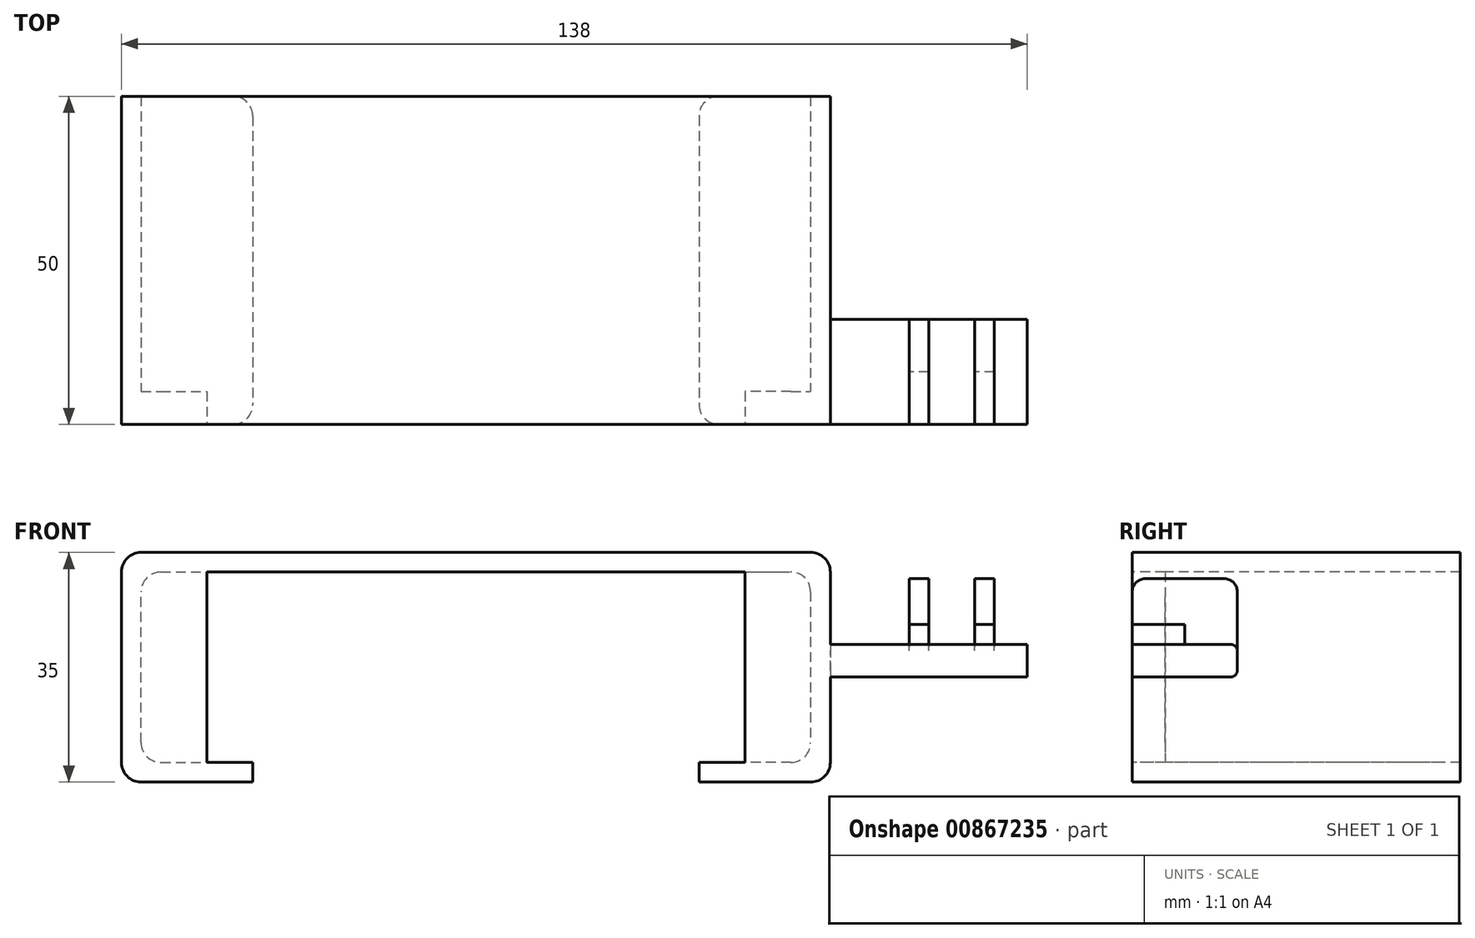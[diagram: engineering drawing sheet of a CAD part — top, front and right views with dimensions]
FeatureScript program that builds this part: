
annotation { "Feature Type Name" : "Feature", "Feature Type Description" : "" }
export const myFeature = defineFeature(function(context is Context, id is Id, definition is map)
    precondition{}
    {
        {
            var Q0;
            Q0=qCreatedBy(makeId("Top.planeOp"),FACE);
            var sketch = newSketch(context, id + "F0", { "sketchPlane" : qUnion([Q0])});
            skLineSegment(sketch, "E0.bottom", {"start": v(-6.5, 16) * mm, "end": v(-3.5, 16) * mm});
            skLineSegment(sketch, "E0.top", {"start": v(-6.5, 0) * mm, "end": v(-3.5, 0) * mm});
            skLineSegment(sketch, "E0.left", {"start": v(-6.5, 16) * mm, "end": v(-6.5, 0) * mm});
            skLineSegment(sketch, "E0.right", {"start": v(-3.5, 16) * mm, "end": v(-3.5, 0) * mm});
            skLineSegment(sketch, "E1.bottom", {"start": v(3.5, 16) * mm, "end": v(6.5, 16) * mm});
            skLineSegment(sketch, "E1.top", {"start": v(3.5, 0) * mm, "end": v(6.5, 0) * mm});
            skLineSegment(sketch, "E1.left", {"start": v(3.5, 16) * mm, "end": v(3.5, 0) * mm});
            skLineSegment(sketch, "E1.right", {"start": v(6.5, 16) * mm, "end": v(6.5, 0) * mm});
            skSolve(sketch);
        }
        {
            var Q0;
            Q0=makeQuery(id+"F0.imprint","IMPRINT",FACE,{"disambiguationData":[TD([[makeQuery(id+"F0.imprint","IMPRINT",EDGE,{"derivedFrom":sQuery(id+"F0.wireOp",EDGE,"E0.bottom")}),-1.0]])]});
            var Q1;
            Q1=makeQuery(id+"F0.imprint","IMPRINT",FACE,{"disambiguationData":[TD([[makeQuery(id+"F0.imprint","IMPRINT",EDGE,{"derivedFrom":sQuery(id+"F0.wireOp",EDGE,"E1.bottom")}),-1.0]])]});
            extrude(context, id + "F1", {"entities" : qUnion([Q0, Q1]), "depth" : 10 * mm, "offsetDistance" : 25 * mm});
        }
        {
            var Q0;
            Q0=makeQuery(id+"F1.opExtrude","SWEPT_FACE",FACE,{"disambiguationData":[OSD([sQuery(id+"F0.wireOp",EDGE,"E0.left")])]});
            var sketch = newSketch(context, id + "F2", { "sketchPlane" : qUnion([Q0])});
            skLineSegment(sketch, "E2.bottom", {"start": v(0, 0) * mm, "end": v(-8, 0) * mm});
            skLineSegment(sketch, "E2.top", {"start": v(0, 3) * mm, "end": v(-8, 3) * mm});
            skLineSegment(sketch, "E2.left", {"start": v(0, 0) * mm, "end": v(0, 3) * mm});
            skLineSegment(sketch, "E2.right", {"start": v(-8, 0) * mm, "end": v(-8, 3) * mm});
            skSolve(sketch);
        }
        {
            var Q0;
            Q0=makeQuery(id+"F2.imprint","IMPRINT",FACE,{"disambiguationData":[TD([[makeQuery(id+"F2.imprint","IMPRINT",EDGE,{"derivedFrom":sQuery(id+"F2.wireOp",EDGE,"E2.bottom")}),1.0]])]});
            extrude(context, id + "F3", {"entities" : qUnion([Q0]), "operationType" : NewBodyOperationType.REMOVE, "oppositeDirection" : true, "depth" : 25 * mm, "offsetDistance" : 25 * mm});
        }
        {
            var Q0;
            Q0=qCreatedBy(makeId("Top.planeOp"),FACE);
            var sketch = newSketch(context, id + "F4", { "sketchPlane" : qUnion([Q0])});
            skPoint(sketch, "E3.0", {"position": v(-6.5, 16) * mm});
            skPoint(sketch, "E4.0", {"position": v(-6.5, 0) * mm});
            skLineSegment(sketch, "E5.bottom", {"start": v(-18.5, 16) * mm, "end": v(11.5, 16) * mm});
            skLineSegment(sketch, "E5.top", {"start": v(-18.5, 0) * mm, "end": v(11.5, 0) * mm});
            skLineSegment(sketch, "E5.left", {"start": v(-18.5, 16) * mm, "end": v(-18.5, 0) * mm});
            skLineSegment(sketch, "E5.right", {"start": v(11.5, 16) * mm, "end": v(11.5, 0) * mm});
            skSolve(sketch);
        }
        {
            var Q0;
            Q0=makeQuery(id+"F4.imprint","IMPRINT",FACE,{"disambiguationData":[TD([[makeQuery(id+"F4.imprint","IMPRINT",EDGE,{"derivedFrom":sQuery(id+"F4.wireOp",EDGE,"E5.bottom")}),-1.0]])]});
            extrude(context, id + "F5", {"entities" : qUnion([Q0]), "operationType" : NewBodyOperationType.ADD, "oppositeDirection" : true, "depth" : 5 * mm, "offsetDistance" : 25 * mm});
        }
        {
            var Q0;
            Q0=qCreatedBy(makeId("Front.planeOp"),FACE);
            var sketch = newSketch(context, id + "F6", { "sketchPlane" : qUnion([Q0])});
            skPoint(sketch, "E6.0", {"position": v(11.5, -5) * mm});
            skPoint(sketch, "E7.0", {"position": v(11.5, 0) * mm});
            skLineSegment(sketch, "E8.right", {"start": v(-123.5, -18) * mm, "end": v(-123.5, 11) * mm});
            skLineSegment(sketch, "E9.bottom", {"start": v(-126.5, 14) * mm, "end": v(-18.5, 14) * mm});
            skLineSegment(sketch, "E9.top", {"start": v(-123.5, 11) * mm, "end": v(-21.5, 11) * mm});
            skLineSegment(sketch, "E10.left", {"start": v(-18.5, 14) * mm, "end": v(-18.5, -21) * mm});
            skLineSegment(sketch, "E10.right", {"start": v(-21.5, 11) * mm, "end": v(-21.5, -18) * mm});
            skLineSegment(sketch, "E11.bottom", {"start": v(-18.5, -21) * mm, "end": v(-38.5, -21) * mm});
            skLineSegment(sketch, "E11.top", {"start": v(-21.5, -18) * mm, "end": v(-38.5, -18) * mm});
            skLineSegment(sketch, "E11.right", {"start": v(-38.5, -21) * mm, "end": v(-38.5, -18) * mm});
            skLineSegment(sketch, "E12.bottom", {"start": v(-126.5, -21) * mm, "end": v(-106.5, -21) * mm});
            skLineSegment(sketch, "E12.top", {"start": v(-123.5, -18) * mm, "end": v(-106.5, -18) * mm});
            skLineSegment(sketch, "E12.right", {"start": v(-106.5, -21) * mm, "end": v(-106.5, -18) * mm});
            skLineSegment(sketch, "E13", {"start": v(-113.5, 11) * mm, "end": v(-113.5, -18) * mm});
            skLineSegment(sketch, "E14", {"start": v(-126.5, -21) * mm, "end": v(-126.5, 14) * mm});
            skLineSegment(sketch, "E15", {"start": v(-31.5, -18) * mm, "end": v(-31.5, 11) * mm});
            skSolve(sketch);
        }
        {
            var Q0;
            {var subQ7=sQuery(id+"F6.wireOp",EDGE,"E8.right");Q0=makeQuery(id+"F6.imprint","IMPRINT",FACE,{"disambiguationData":[TD([[makeQuery(id+"F6.imprint","IMPRINT",EDGE,{"derivedFrom":subQ7}),1.0]])]});}
            extrude(context, id + "F7", {"entities" : qUnion([Q0]), "operationType" : NewBodyOperationType.ADD, "oppositeDirection" : true, "depth" : 50 * mm, "offsetDistance" : 25 * mm});
        }
        {
            var Q0;
            {var subQ0=sQuery(id+"F6.wireOp",EDGE,"E10.right");Q0=makeQuery(id+"F6.imprint","IMPRINT",FACE,{"disambiguationData":[TD([[makeQuery(id+"F6.imprint","IMPRINT",EDGE,{"derivedFrom":subQ0}),-1.0]])]});}
            var Q1;
            {var subQ0=sQuery(id+"F6.wireOp",EDGE,"E8.right");Q1=makeQuery(id+"F6.imprint","IMPRINT",FACE,{"disambiguationData":[TD([[makeQuery(id+"F6.imprint","IMPRINT",EDGE,{"derivedFrom":subQ0}),-1.0]])]});}
            extrude(context, id + "F8", {"entities" : qUnion([Q0, Q1]), "operationType" : NewBodyOperationType.ADD, "oppositeDirection" : true, "depth" : 5 * mm, "offsetDistance" : 25 * mm});
        }
        {
            var Q0;
            Q0=makeQuery(id+"F1.opExtrude","CAP_EDGE",EDGE,{"disambiguationData":[OSD([sQuery(id+"F0.wireOp",EDGE,"E0.bottom")])],"isStart":false});
            var Q1;
            Q1=makeQuery(id+"F1.opExtrude","CAP_EDGE",EDGE,{"disambiguationData":[OSD([sQuery(id+"F0.wireOp",EDGE,"E1.bottom")])],"isStart":false});
            var Q2;
            Q2=makeQuery(id+"F1.opExtrude","CAP_EDGE",EDGE,{"disambiguationData":[OSD([sQuery(id+"F0.wireOp",EDGE,"E0.top")])],"isStart":false});
            var Q3;
            Q3=makeQuery(id+"F1.opExtrude","CAP_EDGE",EDGE,{"disambiguationData":[OSD([sQuery(id+"F0.wireOp",EDGE,"E1.top")])],"isStart":false});
            var Q4;
            {var subQ0=sQuery(id+"F0.wireOp",EDGE,"E0.top");var subQ1=sQuery(id+"F2.wireOp",EDGE,"E2.top");Q4=makeQuery(id+"F3.boolean.opBoolean","COPY",EDGE,{"disambiguationData":[topologyDisambiguationEdgeConnected([makeQuery(id+"F1.opExtrude","SWEPT_FACE",FACE,{"disambiguationData":[OSD([subQ0])]})])],"derivedFrom":makeQuery(id+"F3.opExtrude","SWEPT_EDGE",EDGE,{"disambiguationData":[OSD([subQ0,sQuery(id+"F0.wireOp",EDGE,"E0.left"),subQ1,sQuery(id+"F2.wireOp",EDGE,"E2.left")])]})});}
            var Q5;
            {var subQ0=sQuery(id+"F2.wireOp",EDGE,"E2.top");Q5=makeQuery(id+"F3.boolean.opBoolean","COPY",EDGE,{"disambiguationData":[topologyDisambiguationEdgeConnected([makeQuery(id+"F1.opExtrude","SWEPT_FACE",FACE,{"disambiguationData":[OSD([sQuery(id+"F0.wireOp",EDGE,"E1.top")])]})])],"derivedFrom":makeQuery(id+"F3.opExtrude","SWEPT_EDGE",EDGE,{"disambiguationData":[OSD([sQuery(id+"F0.wireOp",EDGE,"E0.top"),sQuery(id+"F0.wireOp",EDGE,"E0.left"),subQ0,sQuery(id+"F2.wireOp",EDGE,"E2.left")])]})});}
            fillet(context, id + "F9", {"entities" : qUnion([Q0, Q1, Q2, Q3, Q4, Q5]), "radius" : 2 * mm, "tangentPropagation" : true, "allowEdgeOverflow" : false});
        }
        {
            var Q0;
            Q0=makeQuery(id+"F7.opExtrude","SWEPT_EDGE",EDGE,{"disambiguationData":[OSD([sQuery(id+"F6.wireOp",EDGE,"E9.top"),sQuery(id+"F6.wireOp",EDGE,"E10.right")])]});
            var Q1;
            Q1=makeQuery(id+"F7.opExtrude","SWEPT_EDGE",EDGE,{"disambiguationData":[OSD([sQuery(id+"F6.wireOp",EDGE,"E8.right"),sQuery(id+"F6.wireOp",EDGE,"E9.top")])]});
            var Q2;
            Q2=makeQuery(id+"F7.opExtrude","SWEPT_EDGE",EDGE,{"disambiguationData":[OSD([sQuery(id+"F6.wireOp",EDGE,"E9.bottom"),sQuery(id+"F6.wireOp",EDGE,"E14")])]});
            var Q3;
            Q3=makeQuery(id+"F7.opExtrude","SWEPT_EDGE",EDGE,{"disambiguationData":[OSD([sQuery(id+"F6.wireOp",EDGE,"E9.bottom"),sQuery(id+"F6.wireOp",EDGE,"E10.left")])]});
            var Q4;
            Q4=makeQuery(id+"F7.opExtrude","SWEPT_EDGE",EDGE,{"disambiguationData":[OSD([sQuery(id+"F6.wireOp",EDGE,"E10.left"),sQuery(id+"F6.wireOp",EDGE,"E11.bottom")])]});
            var Q5;
            Q5=makeQuery(id+"F7.opExtrude","SWEPT_EDGE",EDGE,{"disambiguationData":[OSD([sQuery(id+"F6.wireOp",EDGE,"E10.right"),sQuery(id+"F6.wireOp",EDGE,"E11.top")])]});
            var Q6;
            Q6=makeQuery(id+"F7.opExtrude","SWEPT_EDGE",EDGE,{"disambiguationData":[OSD([sQuery(id+"F6.wireOp",EDGE,"E8.right"),sQuery(id+"F6.wireOp",EDGE,"E12.top")])]});
            var Q7;
            Q7=makeQuery(id+"F7.opExtrude","SWEPT_EDGE",EDGE,{"disambiguationData":[OSD([sQuery(id+"F6.wireOp",EDGE,"E12.bottom"),sQuery(id+"F6.wireOp",EDGE,"E14")])]});
            var Q8;
            Q8=makeQuery(id+"F8.opExtrude","CAP_EDGE",EDGE,{"disambiguationData":[OSD([sQuery(id+"F6.wireOp",EDGE,"E8.right")])],"isStart":false});
            var Q9;
            Q9=makeQuery(id+"F8.opExtrude","CAP_EDGE",EDGE,{"disambiguationData":[OSD([sQuery(id+"F6.wireOp",EDGE,"E12.top")])],"isStart":false});
            var Q10;
            Q10=makeQuery(id+"F8.opExtrude","CAP_EDGE",EDGE,{"disambiguationData":[OSD([sQuery(id+"F6.wireOp",EDGE,"E11.top")])],"isStart":false});
            var Q11;
            Q11=makeQuery(id+"F8.opExtrude","CAP_EDGE",EDGE,{"disambiguationData":[OSD([sQuery(id+"F6.wireOp",EDGE,"E10.right")])],"isStart":false});
            var Q12;
            {var subQ0=sQuery(id+"F6.wireOp",EDGE,"E9.top");Q12=makeQuery(id+"F8.opExtrude","CAP_EDGE",EDGE,{"disambiguationData":[OSD([subQ0]),TDD([makeQuery(id+"F6.imprint","IMPRINT",EDGE,{"disambiguationData":[TD([[makeQuery(id+"F6.imprint","INTERSECT",VERTEX,{"derivedFrom":[subQ0,sQuery(id+"F6.wireOp",EDGE,"E10.right")]}),1.0]])],"derivedFrom":subQ0})])],"isStart":false});}
            var Q13;
            {var subQ0=sQuery(id+"F6.wireOp",EDGE,"E9.top");Q13=makeQuery(id+"F8.opExtrude","CAP_EDGE",EDGE,{"disambiguationData":[OSD([subQ0]),TDD([makeQuery(id+"F6.imprint","IMPRINT",EDGE,{"disambiguationData":[TD([[makeQuery(id+"F6.imprint","INTERSECT",VERTEX,{"derivedFrom":[sQuery(id+"F6.wireOp",EDGE,"E8.right"),subQ0]}),-1.0]])],"derivedFrom":subQ0})])],"isStart":false});}
            var Q14;
            Q14=makeQuery(id+"F7.opExtrude","CAP_EDGE",EDGE,{"disambiguationData":[OSD([sQuery(id+"F6.wireOp",EDGE,"E11.right")])],"isStart":true});
            var Q15;
            Q15=makeQuery(id+"F7.opExtrude","CAP_EDGE",EDGE,{"disambiguationData":[OSD([sQuery(id+"F6.wireOp",EDGE,"E12.right")])],"isStart":true});
            var Q16;
            Q16=makeQuery(id+"F7.opExtrude","CAP_EDGE",EDGE,{"disambiguationData":[OSD([sQuery(id+"F6.wireOp",EDGE,"E11.right")])],"isStart":false});
            var Q17;
            Q17=makeQuery(id+"F7.opExtrude","CAP_EDGE",EDGE,{"disambiguationData":[OSD([sQuery(id+"F6.wireOp",EDGE,"E12.right")])],"isStart":false});
            fillet(context, id + "F10", {"entities" : qUnion([Q0, Q1, Q2, Q3, Q4, Q5, Q6, Q7, Q8, Q9, Q10, Q11, Q12, Q13, Q14, Q15, Q16, Q17]), "radius" : 3 * mm, "tangentPropagation" : true, "allowEdgeOverflow" : false});
        }
        {
            var Q0;
            Q0=makeQuery(id+"F5.opExtrude","SWEPT_EDGE",EDGE,{"disambiguationData":[OSD([sQuery(id+"F4.wireOp",EDGE,"E5.bottom"),sQuery(id+"F4.wireOp",EDGE,"E5.left")])]});
            var Q1;
            Q1=makeQuery(id+"F5.opExtrude","CAP_EDGE",EDGE,{"disambiguationData":[OSD([sQuery(id+"F4.wireOp",EDGE,"E5.bottom")])],"isStart":false});
            var Q2;
            {var subQ0=sQuery(id+"F4.wireOp",EDGE,"E5.bottom");Q2=makeQuery(id+"F5.boolean.opBoolean","SPLIT",EDGE,{"disambiguationData":[TD([makeQuery(id+"F1.opExtrude","SWEPT_FACE",FACE,{"disambiguationData":[OSD([sQuery(id+"F0.wireOp",EDGE,"E0.left")])]})])],"derivedFrom":makeQuery(id+"F5.opExtrude","CAP_EDGE",EDGE,{"disambiguationData":[OSD([subQ0])],"isStart":true})});}
            var Q3;
            {var subQ0=sQuery(id+"F4.wireOp",EDGE,"E5.bottom");Q3=makeQuery(id+"F5.boolean.opBoolean","SPLIT",EDGE,{"disambiguationData":[TD([makeQuery(id+"F1.opExtrude","SWEPT_FACE",FACE,{"disambiguationData":[OSD([sQuery(id+"F0.wireOp",EDGE,"E0.right")])]})])],"derivedFrom":makeQuery(id+"F5.opExtrude","CAP_EDGE",EDGE,{"disambiguationData":[OSD([subQ0])],"isStart":true})});}
            var Q4;
            {var subQ0=sQuery(id+"F4.wireOp",EDGE,"E5.bottom");Q4=makeQuery(id+"F5.boolean.opBoolean","SPLIT",EDGE,{"disambiguationData":[TD([makeQuery(id+"F1.opExtrude","SWEPT_FACE",FACE,{"disambiguationData":[OSD([sQuery(id+"F0.wireOp",EDGE,"E1.right")])]})])],"derivedFrom":makeQuery(id+"F5.opExtrude","CAP_EDGE",EDGE,{"disambiguationData":[OSD([subQ0])],"isStart":true})});}
            fillet(context, id + "F11", {"entities" : qUnion([Q0, Q1, Q2, Q3, Q4]), "radius" : 1 * mm, "tangentPropagation" : true, "allowEdgeOverflow" : false});
        }
    });
